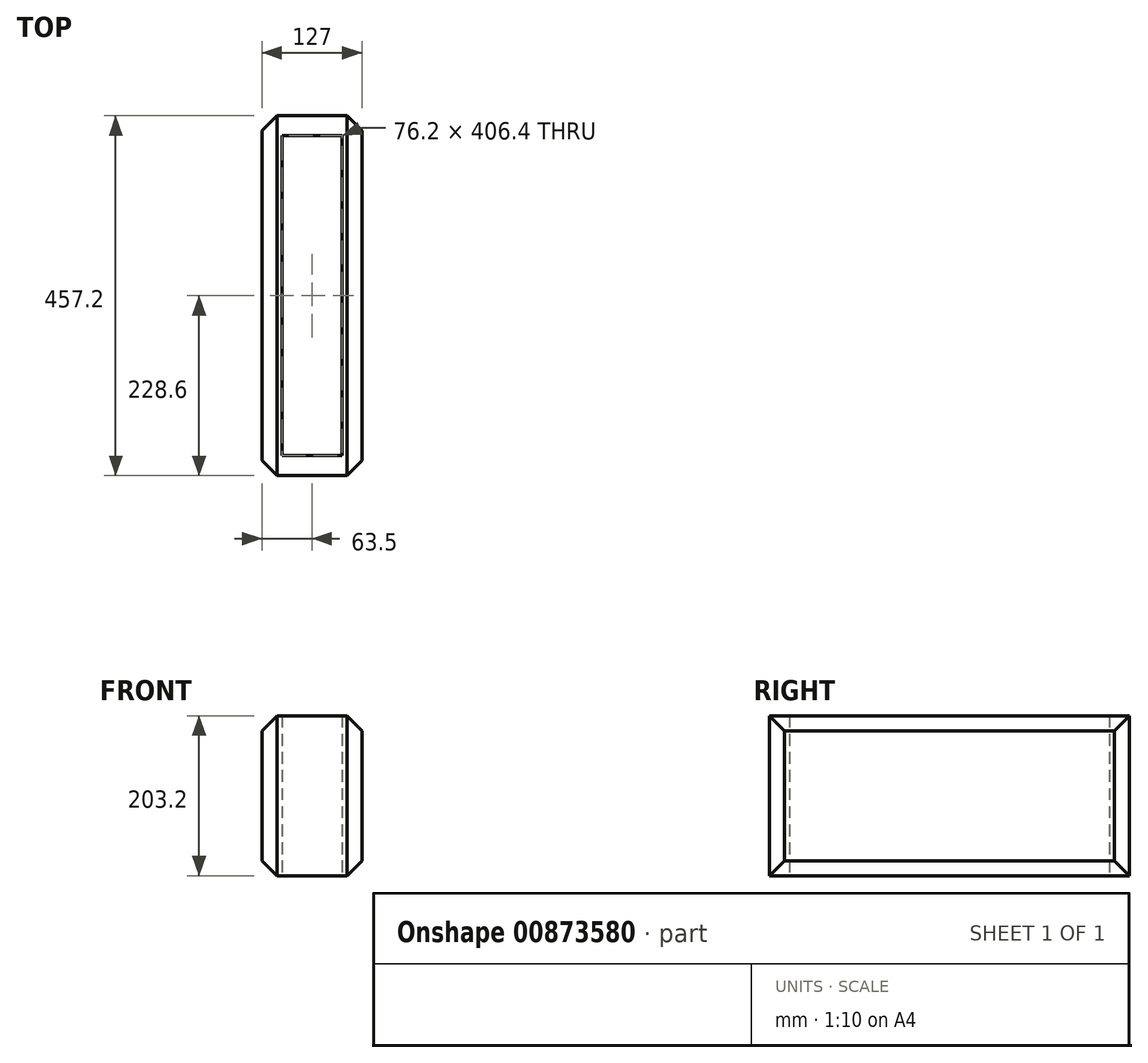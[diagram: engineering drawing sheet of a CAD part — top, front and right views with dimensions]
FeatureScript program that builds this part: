
annotation { "Feature Type Name" : "Feature", "Feature Type Description" : "" }
export const myFeature = defineFeature(function(context is Context, id is Id, definition is map)
    precondition{}
    {
        {
            var Q0;
            Q0=qCreatedBy(makeId("Top.planeOp"),FACE);
            var sketch = newSketch(context, id + "F0", { "sketchPlane" : qUnion([Q0])});
            skLineSegment(sketch, "E0.bottom", {"start": v(0, 0) * mm, "end": v(127, 0) * mm});
            skLineSegment(sketch, "E0.top", {"start": v(0, 457.2) * mm, "end": v(127, 457.2) * mm});
            skLineSegment(sketch, "E0.left", {"start": v(0, 0) * mm, "end": v(0, 457.2) * mm});
            skLineSegment(sketch, "E0.right", {"start": v(127, 0) * mm, "end": v(127, 457.2) * mm});
            skLineSegment(sketch, "E1.0", {"start": v(25.4, 25.4) * mm, "end": v(101.6, 25.4) * mm});
            skLineSegment(sketch, "E1.1", {"start": v(25.4, 25.4) * mm, "end": v(25.4, 431.8) * mm});
            skLineSegment(sketch, "E1.2", {"start": v(25.4, 431.8) * mm, "end": v(101.6, 431.8) * mm});
            skLineSegment(sketch, "E1.3", {"start": v(101.6, 25.4) * mm, "end": v(101.6, 431.8) * mm});
            skSolve(sketch);
        }
        {
            var Q0;
            Q0 = qSketchRegion(id + "F0", true);
            extrude(context, id + "F1", {"entities" : qUnion([Q0]), "depth" : 203.2 * mm, "offsetDistance" : 25.4 * mm});
        }
        {
            var Q0;
            Q0=makeQuery(id+"F1.opExtrude","CAP_EDGE",EDGE,{"disambiguationData":[OSD([sQuery(id+"F0.wireOp",EDGE,"E0.right")])],"isStart":false});
            var Q1;
            Q1=makeQuery(id+"F1.opExtrude","CAP_EDGE",EDGE,{"disambiguationData":[OSD([sQuery(id+"F0.wireOp",EDGE,"E0.right")])],"isStart":true});
            var Q2;
            Q2=makeQuery(id+"F1.opExtrude","CAP_EDGE",EDGE,{"disambiguationData":[OSD([sQuery(id+"F0.wireOp",EDGE,"E0.left")])],"isStart":false});
            var Q3;
            Q3=makeQuery(id+"F1.opExtrude","CAP_EDGE",EDGE,{"disambiguationData":[OSD([sQuery(id+"F0.wireOp",EDGE,"E0.left")])],"isStart":true});
            var Q4;
            Q4=makeQuery(id+"F1.opExtrude","SWEPT_EDGE",EDGE,{"disambiguationData":[OSD([sQuery(id+"F0.wireOp",EDGE,"E0.bottom"),sQuery(id+"F0.wireOp",EDGE,"E0.right")])]});
            var Q5;
            Q5=makeQuery(id+"F1.opExtrude","SWEPT_EDGE",EDGE,{"disambiguationData":[OSD([sQuery(id+"F0.wireOp",EDGE,"E0.bottom"),sQuery(id+"F0.wireOp",EDGE,"E0.left")])]});
            var Q6;
            Q6=makeQuery(id+"F1.opExtrude","SWEPT_EDGE",EDGE,{"disambiguationData":[OSD([sQuery(id+"F0.wireOp",EDGE,"E0.top"),sQuery(id+"F0.wireOp",EDGE,"E0.right")])]});
            var Q7;
            Q7=makeQuery(id+"F1.opExtrude","SWEPT_EDGE",EDGE,{"disambiguationData":[OSD([sQuery(id+"F0.wireOp",EDGE,"E0.top"),sQuery(id+"F0.wireOp",EDGE,"E0.left")])]});
            chamfer(context, id + "F2", {"entities" : qUnion([Q0, Q1, Q2, Q3, Q4, Q5, Q6, Q7]), "width" : 19.05 * mm, "tangentPropagation" : true});
        }
    });
